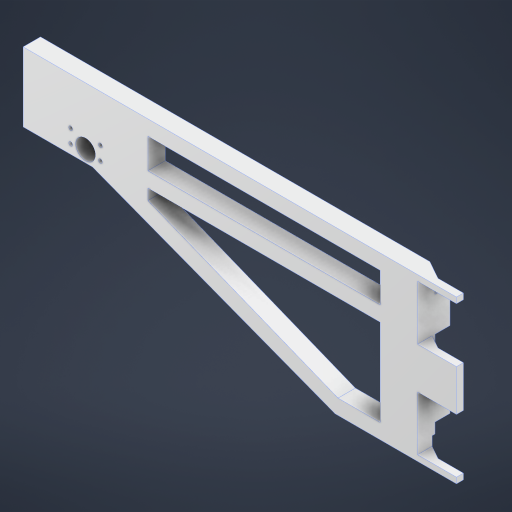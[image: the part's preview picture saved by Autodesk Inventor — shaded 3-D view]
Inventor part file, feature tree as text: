
AUTODESK INVENTOR PART (.ipt)
format: ipt  version: 2024 (Build 280153000, 153)  size: 443,392 bytes
history: native  units: mm
features: sketch x13, extrude x11, other x1, fillet x1
ambient origin geometry x8: Origin, YZ Plane, XZ Plane, XY Plane, X Axis, Y Axis, Z Axis, Center Point
bodies: Body1 (feature_tree)
feature tree (26):
  other  "Твердое тело1"
  extrude  "Выдавливание1"  Depth=10.0mm
  extrude  "Выдавливание2"  Depth=650.0mm
  sketch  "Эскиз3"
  sketch  "Эскиз4"
  sketch  "Эскиз5"
  extrude  "Выдавливание3"  Depth=280.0mm TaperAngle=0.0deg
  extrude  "Выдавливание4"  Depth=120.0mm
  fillet  "Сопряжение1"  Radius=120.0mm
  extrude  "Выдавливание5"  Depth=55.0mm TaperAngle=0.0deg
  extrude  "Extrusion13"  Depth=3.0mm
  sketch  "Sketch16"  dims[d2=650.0mm d3=650.0mm]
  extrude  "Extrusion14"  Depth=100.0mm TaperAngle=0.0deg
  extrude  "Extrusion15"  Depth=26.0mm
  extrude  "Extrusion16"  Depth=26.0mm
  extrude  "Extrusion17"  Depth=20.0mm TaperAngle=0.0deg
  extrude  "Extrusion18"  TaperAngle=0.0deg  [1 undecoded]
  sketch  "Эскиз1"
  sketch  "Эскиз2"
  sketch  "Эскиз6"
  sketch  "Sketch14"  dims[d0=20.0mm d1=10.0mm]
  sketch  "Sketch17"  dims[d4=0.0mm d5=280.0mm d6=0.0mm]
  sketch  "Sketch18"  dims[d7=99.0mm d8=0.0mm d9=120.0mm d10=120.0mm]
  sketch  "Sketch19"  dims[d11=4.25mm d12=4.25mm d13=4.25mm d14=4.25mm d15=19.0mm d16=34.0mm]
  sketch  "Sketch20"  dims[d17=4.25mm d18=4.25mm d19=4.25mm d20=4.25mm d21=19.0mm d22=34.0mm d23=55.0mm d24=0.0mm]
  sketch  "Sketch21"  dims[d25=5.0mm d26=0.0mm d27=3.0mm d28=100.0mm d29=0.0mm d54=26.0mm d55=26.0mm d56=20.0mm d57=0.0mm d58=0.0mm d59=100.0mm d60=0.0mm d61=26.344949mm d64=10.0mm d65=10.0mm d66=30.0mm d67=0.0mm d68=73.0mm d69=52.0mm d70=52.0mm d71=1000.0mm d72=0.0mm d73=78.0mm d74=78.0mm d75=0.0mm d76=0.0mm d77=19.0mm d79=94.0mm d80=50.0mm d81=10.0mm d82=0.0mm d83=55.0mm d84=55.0mm d85=60.0mm d86=60.0mm d87=26.0mm d88=0.0mm]
note: 1 required parameter value undecoded (feature->parameter linkage not recoverable at this tier; creation-order binding heuristic only, values carry confidence <= 0.55)
